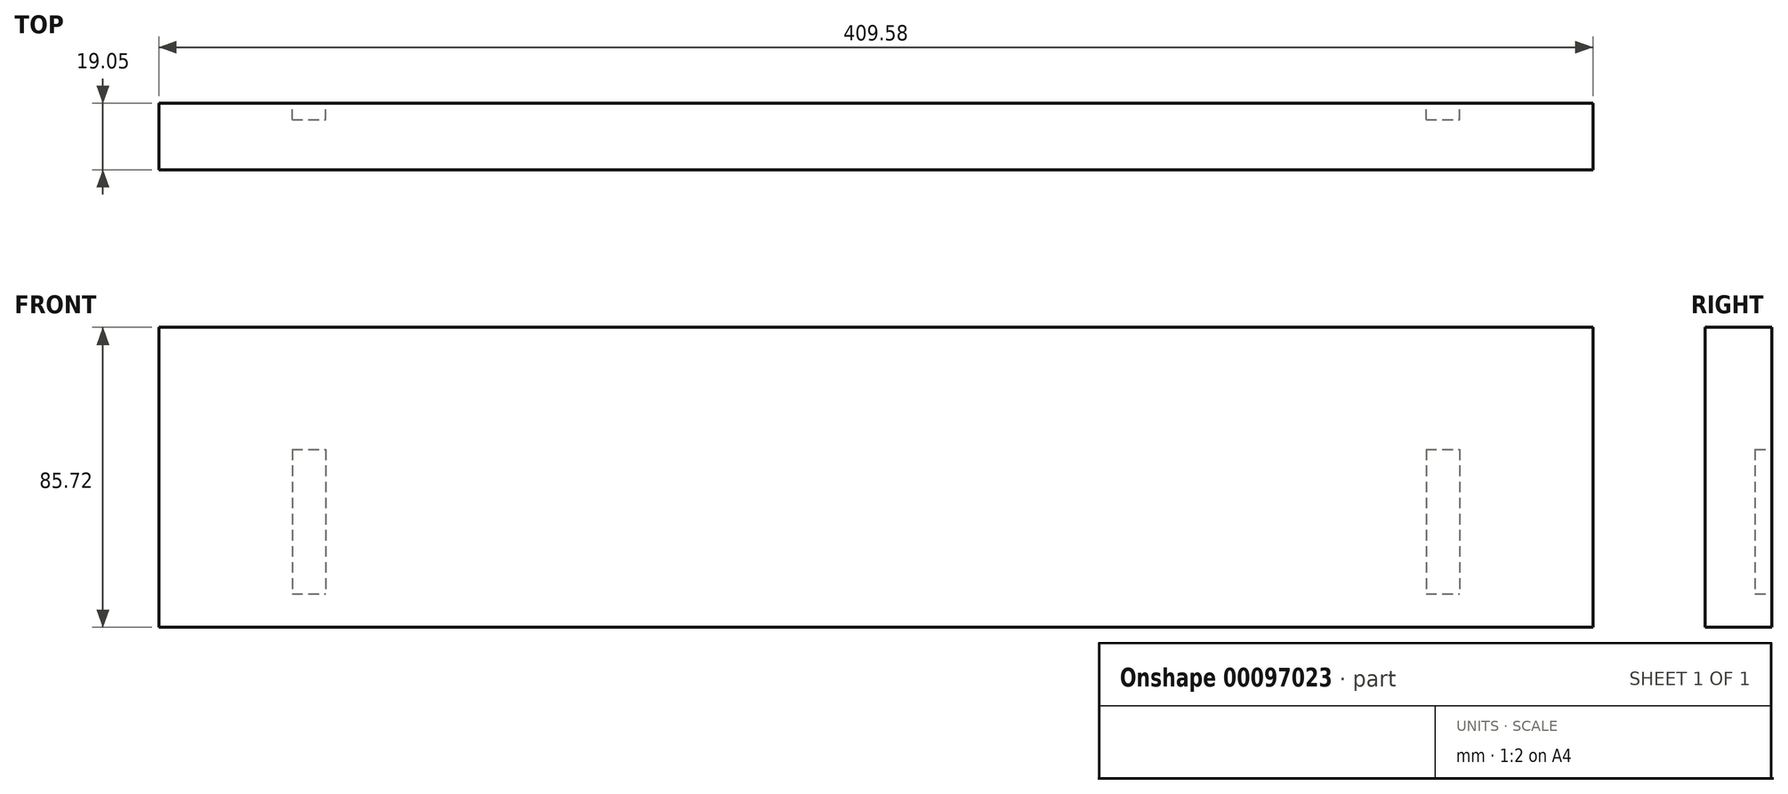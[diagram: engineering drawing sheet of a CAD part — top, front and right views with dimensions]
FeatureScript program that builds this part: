
annotation { "Feature Type Name" : "Feature", "Feature Type Description" : "" }
export const myFeature = defineFeature(function(context is Context, id is Id, definition is map)
    precondition{}
    {
        {
            var Q0;
            Q0=qCreatedBy(makeId("Front.planeOp"),FACE);
            var sketch = newSketch(context, id + "F0", { "sketchPlane" : qUnion([Q0])});
            skLineSegment(sketch, "E0.bottom", {"start": v(-204.79, 42.86) * mm, "end": v(204.79, 42.86) * mm});
            skLineSegment(sketch, "E0.top", {"start": v(-204.79, -42.86) * mm, "end": v(204.79, -42.86) * mm});
            skLineSegment(sketch, "E0.left", {"start": v(-204.79, 42.86) * mm, "end": v(-204.79, -42.86) * mm});
            skLineSegment(sketch, "E0.right", {"start": v(204.79, 42.86) * mm, "end": v(204.79, -42.86) * mm});
            skPoint(sketch, "E0.middle", {"position": v(0, 0) * mm});
            skLineSegment(sketch, "E1.0", {"start": v(-166.69, 7.94) * mm, "end": v(-166.69, -33.34) * mm});
            skLineSegment(sketch, "E2.0", {"start": v(166.69, 7.94) * mm, "end": v(166.69, -33.34) * mm});
            skLineSegment(sketch, "E3.0", {"start": v(-166.69, -33.34) * mm, "end": v(-157.16, -33.34) * mm});
            skLineSegment(sketch, "E4.0", {"start": v(-166.69, 7.94) * mm, "end": v(-157.16, 7.94) * mm});
            skLineSegment(sketch, "E5.0", {"start": v(-157.16, 7.94) * mm, "end": v(-157.16, -33.34) * mm});
            skLineSegment(sketch, "E6.0", {"start": v(157.16, 7.94) * mm, "end": v(157.16, -33.34) * mm});
            skLineSegment(sketch, "E7.trimOffspring", {"start": v(157.16, 7.94) * mm, "end": v(166.69, 7.94) * mm});
            skLineSegment(sketch, "E8.trimOffspring", {"start": v(157.16, -33.34) * mm, "end": v(166.69, -33.34) * mm});
            skSolve(sketch);
        }
        {
            var Q0;
            Q0=makeQuery(id+"F0.imprint","IMPRINT",FACE,{"disambiguationData":[TD([[makeQuery(id+"F0.imprint","IMPRINT",EDGE,{"derivedFrom":sQuery(id+"F0.wireOp",EDGE,"E0.bottom")}),-1.0]])]});
            var Q1;
            Q1=makeQuery(id+"F0.imprint","IMPRINT",FACE,{"disambiguationData":[TD([[makeQuery(id+"F0.imprint","IMPRINT",EDGE,{"derivedFrom":sQuery(id+"F0.wireOp",EDGE,"E2.0")}),-1.0]])]});
            var Q2;
            Q2=makeQuery(id+"F0.imprint","IMPRINT",FACE,{"disambiguationData":[TD([[makeQuery(id+"F0.imprint","IMPRINT",EDGE,{"derivedFrom":sQuery(id+"F0.wireOp",EDGE,"E1.0")}),1.0]])]});
            extrude(context, id + "F1", {"entities" : qUnion([Q0, Q1, Q2]), "depth" : 19.05 * mm});
        }
        {
            var Q0;
            Q0=makeQuery(id+"F0.imprint","IMPRINT",FACE,{"disambiguationData":[TD([[makeQuery(id+"F0.imprint","IMPRINT",EDGE,{"derivedFrom":sQuery(id+"F0.wireOp",EDGE,"E2.0")}),-1.0]])]});
            var Q1;
            Q1=makeQuery(id+"F0.imprint","IMPRINT",FACE,{"disambiguationData":[TD([[makeQuery(id+"F0.imprint","IMPRINT",EDGE,{"derivedFrom":sQuery(id+"F0.wireOp",EDGE,"E1.0")}),1.0]])]});
            extrude(context, id + "F2", {"entities" : qUnion([Q0, Q1]), "operationType" : NewBodyOperationType.REMOVE, "depth" : 4.76 * mm});
        }
    });
